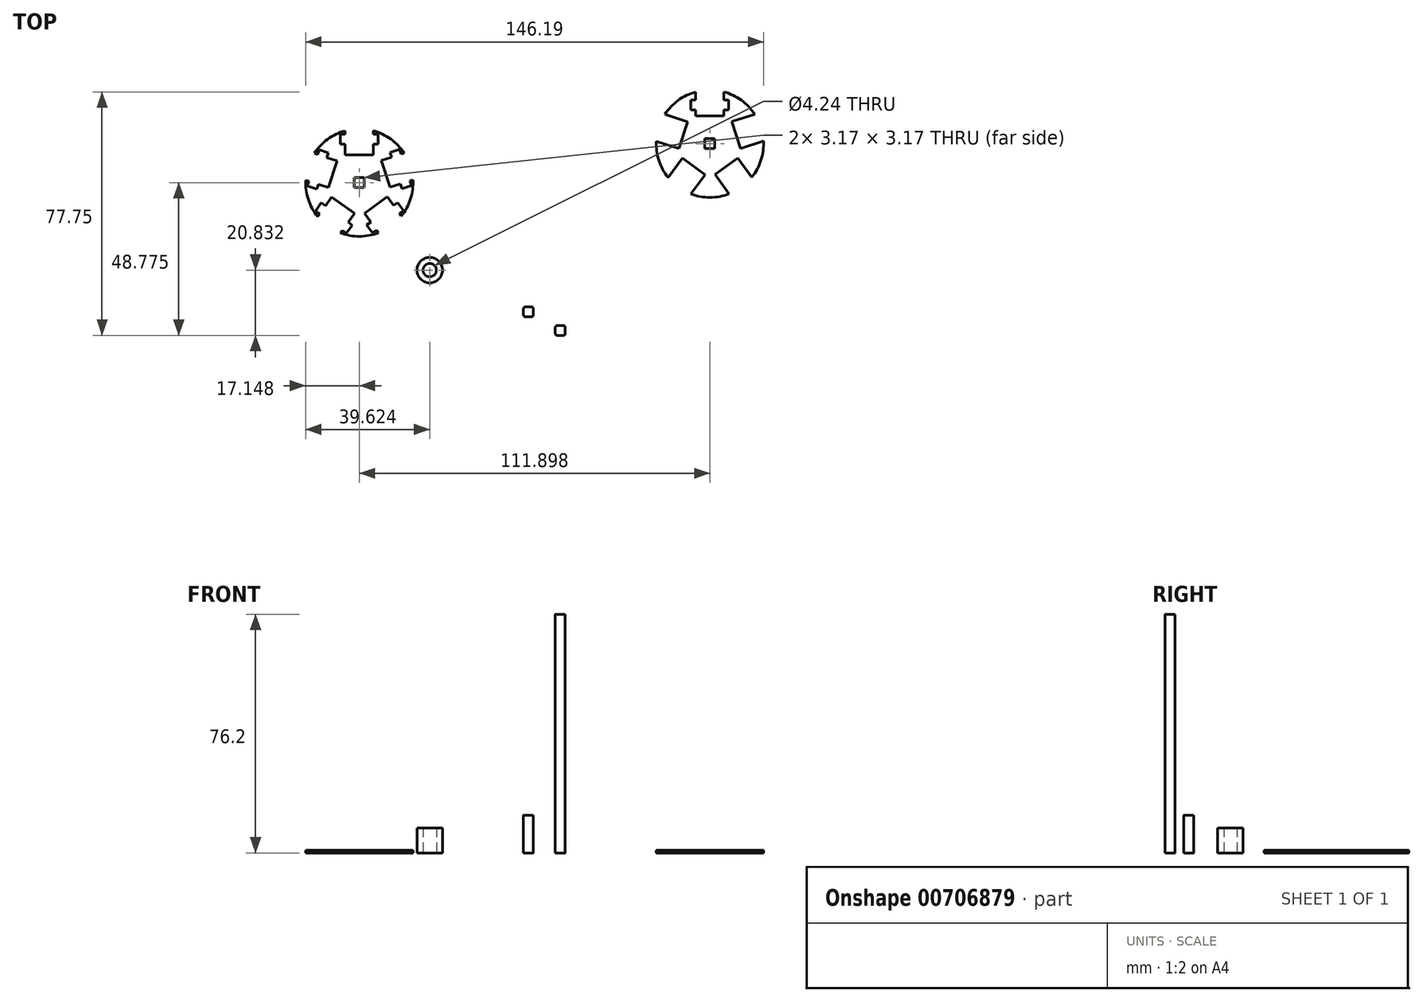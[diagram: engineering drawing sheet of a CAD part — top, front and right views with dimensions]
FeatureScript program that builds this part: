
annotation { "Feature Type Name" : "Feature", "Feature Type Description" : "" }
export const myFeature = defineFeature(function(context is Context, id is Id, definition is map)
    precondition{}
    {
        {
            var Q0;
            Q0=qCreatedBy(makeId("Top.planeOp"),FACE);
            var sketch = newSketch(context, id + "F0", { "sketchPlane" : qUnion([Q0])});
            skCircle(sketch, "E0", {"center": v(-23.39, -16.05) * mm, "radius": 4.06 * mm});
            skCircle(sketch, "E1", {"center": v(-23.39, -16.05) * mm, "radius": 2.12 * mm});
            skLineSegment(sketch, "E2.bottom", {"start": v(-44.27, 10.3) * mm, "end": v(-47.45, 10.3) * mm});
            skLineSegment(sketch, "E2.top", {"start": v(-44.27, 13.48) * mm, "end": v(-47.45, 13.48) * mm});
            skLineSegment(sketch, "E2.left", {"start": v(-44.27, 10.3) * mm, "end": v(-44.27, 13.48) * mm});
            skLineSegment(sketch, "E2.right", {"start": v(-47.45, 10.3) * mm, "end": v(-47.45, 13.48) * mm});
            skPoint(sketch, "E2.middle", {"position": v(-45.86, 11.9) * mm});
            skCircle(sketch, "E3", {"center": v(-45.86, 11.9) * mm, "radius": 17.15 * mm});
            skLineSegment(sketch, "E4.bottom", {"start": v(-41.42, 20.79) * mm, "end": v(-50.42, 20.79) * mm});
            skLineSegment(sketch, "E4.top", {"start": v(-41.42, 37.3) * mm, "end": v(-50.42, 37.3) * mm});
            skLineSegment(sketch, "E4.left", {"start": v(-41.42, 20.79) * mm, "end": v(-41.42, 37.3) * mm});
            skLineSegment(sketch, "E4.right", {"start": v(-50.42, 20.79) * mm, "end": v(-50.42, 37.3) * mm});
            skPoint(sketch, "E4.middle", {"position": v(-45.92, 29.04) * mm});
            skPoint(sketch, "E5.center", {"position": v(-54.13, 17) * mm});
            skLineSegment(sketch, "E6.bottom", {"start": v(-50.42, 27.39) * mm, "end": v(-52, 27.39) * mm});
            skLineSegment(sketch, "E6.top", {"start": v(-50.42, 24.21) * mm, "end": v(-52, 24.21) * mm});
            skLineSegment(sketch, "E6.left", {"start": v(-50.42, 27.39) * mm, "end": v(-50.42, 24.21) * mm});
            skLineSegment(sketch, "E6.right", {"start": v(-52, 27.39) * mm, "end": v(-52, 24.21) * mm});
            skLineSegment(sketch, "E7.bottom", {"start": v(-41.42, 27.39) * mm, "end": v(-39.83, 27.39) * mm});
            skLineSegment(sketch, "E7.top", {"start": v(-41.42, 24.21) * mm, "end": v(-39.83, 24.21) * mm});
            skLineSegment(sketch, "E7.left", {"start": v(-41.42, 27.39) * mm, "end": v(-41.42, 24.21) * mm});
            skLineSegment(sketch, "E7.right", {"start": v(-39.83, 27.39) * mm, "end": v(-39.83, 24.21) * mm});
            skLineSegment(sketch, "E8.1.0", {"start": v(-38.81, 18.97) * mm, "end": v(-23.11, 24.08) * mm});
            skLineSegment(sketch, "E8.1.1", {"start": v(-36.03, 10.41) * mm, "end": v(-20.33, 15.52) * mm});
            skLineSegment(sketch, "E8.1.2", {"start": v(-36.03, 10.41) * mm, "end": v(-38.81, 18.97) * mm});
            skLineSegment(sketch, "E8.1.3", {"start": v(-32.77, 11.47) * mm, "end": v(-32.28, 9.96) * mm});
            skLineSegment(sketch, "E8.1.4", {"start": v(-29.75, 12.46) * mm, "end": v(-29.26, 10.95) * mm});
            skLineSegment(sketch, "E8.1.5", {"start": v(-29.26, 10.95) * mm, "end": v(-32.28, 9.96) * mm});
            skLineSegment(sketch, "E8.1.6", {"start": v(-35.55, 20.03) * mm, "end": v(-36.04, 21.54) * mm});
            skLineSegment(sketch, "E8.1.7", {"start": v(-33.02, 22.52) * mm, "end": v(-36.04, 21.54) * mm});
            skLineSegment(sketch, "E8.1.8", {"start": v(-32.53, 21.01) * mm, "end": v(-33.02, 22.52) * mm});
            skLineSegment(sketch, "E8.2.0", {"start": v(-36.95, 7.38) * mm, "end": v(-27.25, -5.98) * mm});
            skLineSegment(sketch, "E8.2.1", {"start": v(-44.23, 2.1) * mm, "end": v(-34.53, -11.27) * mm});
            skLineSegment(sketch, "E8.2.2", {"start": v(-44.23, 2.1) * mm, "end": v(-36.95, 7.38) * mm});
            skLineSegment(sketch, "E8.2.3", {"start": v(-42.22, -0.68) * mm, "end": v(-43.5, -1.62) * mm});
            skLineSegment(sketch, "E8.2.4", {"start": v(-40.35, -3.25) * mm, "end": v(-41.64, -4.19) * mm});
            skLineSegment(sketch, "E8.2.5", {"start": v(-41.64, -4.19) * mm, "end": v(-43.5, -1.62) * mm});
            skLineSegment(sketch, "E8.2.6", {"start": v(-34.94, 4.6) * mm, "end": v(-33.65, 5.54) * mm});
            skLineSegment(sketch, "E8.2.7", {"start": v(-31.79, 2.97) * mm, "end": v(-33.65, 5.54) * mm});
            skLineSegment(sketch, "E8.2.8", {"start": v(-33.07, 2.04) * mm, "end": v(-31.79, 2.97) * mm});
            skLineSegment(sketch, "E8.3.0", {"start": v(-47.4, 2.03) * mm, "end": v(-57.1, -11.33) * mm});
            skLineSegment(sketch, "E8.3.1", {"start": v(-54.68, 7.32) * mm, "end": v(-64.39, -6.04) * mm});
            skLineSegment(sketch, "E8.3.2", {"start": v(-54.68, 7.32) * mm, "end": v(-47.4, 2.03) * mm});
            skLineSegment(sketch, "E8.3.3", {"start": v(-56.7, 4.54) * mm, "end": v(-57.98, 5.48) * mm});
            skLineSegment(sketch, "E8.3.4", {"start": v(-58.57, 1.97) * mm, "end": v(-59.85, 2.9) * mm});
            skLineSegment(sketch, "E8.3.5", {"start": v(-59.85, 2.9) * mm, "end": v(-57.98, 5.48) * mm});
            skLineSegment(sketch, "E8.3.6", {"start": v(-49.42, -0.75) * mm, "end": v(-48.13, -1.68) * mm});
            skLineSegment(sketch, "E8.3.7", {"start": v(-50, -4.25) * mm, "end": v(-48.13, -1.68) * mm});
            skLineSegment(sketch, "E8.3.8", {"start": v(-51.28, -3.32) * mm, "end": v(-50, -4.25) * mm});
            skLineSegment(sketch, "E8.4.0", {"start": v(-55.72, 10.31) * mm, "end": v(-71.43, 15.41) * mm});
            skLineSegment(sketch, "E8.4.1", {"start": v(-52.94, 18.87) * mm, "end": v(-68.65, 23.97) * mm});
            skLineSegment(sketch, "E8.4.2", {"start": v(-52.94, 18.87) * mm, "end": v(-55.72, 10.31) * mm});
            skLineSegment(sketch, "E8.4.3", {"start": v(-56.2, 19.93) * mm, "end": v(-55.71, 21.44) * mm});
            skLineSegment(sketch, "E8.4.4", {"start": v(-59.22, 20.91) * mm, "end": v(-58.73, 22.42) * mm});
            skLineSegment(sketch, "E8.4.5", {"start": v(-58.73, 22.42) * mm, "end": v(-55.71, 21.44) * mm});
            skLineSegment(sketch, "E8.4.6", {"start": v(-58.99, 11.37) * mm, "end": v(-59.48, 9.86) * mm});
            skLineSegment(sketch, "E8.4.7", {"start": v(-62.5, 10.84) * mm, "end": v(-59.48, 9.86) * mm});
            skLineSegment(sketch, "E8.4.8", {"start": v(-62, 12.35) * mm, "end": v(-62.5, 10.84) * mm});
            skLineSegment(sketch, "E8.anchor1", {"start": v(-45.86, 11.9) * mm, "end": v(-50.42, 20.79) * mm, "construction": true});
            skLineSegment(sketch, "E8.anchor2", {"start": v(-45.86, 11.9) * mm, "end": v(-50.42, 20.79) * mm, "construction": true});
            skLineSegment(sketch, "E9.bottom", {"start": v(67.62, 22.73) * mm, "end": v(64.45, 22.73) * mm});
            skLineSegment(sketch, "E9.top", {"start": v(67.62, 25.9) * mm, "end": v(64.45, 25.9) * mm});
            skLineSegment(sketch, "E9.left", {"start": v(67.62, 22.73) * mm, "end": v(67.62, 25.9) * mm});
            skLineSegment(sketch, "E9.right", {"start": v(64.45, 22.73) * mm, "end": v(64.45, 25.9) * mm});
            skPoint(sketch, "E9.middle", {"position": v(66.04, 24.32) * mm});
            skCircle(sketch, "E10", {"center": v(66.04, 24.32) * mm, "radius": 17.15 * mm});
            skLineSegment(sketch, "E11.bottom", {"start": v(70.48, 33.2) * mm, "end": v(61.48, 33.2) * mm});
            skLineSegment(sketch, "E11.top", {"start": v(70.48, 49.72) * mm, "end": v(61.48, 49.72) * mm});
            skLineSegment(sketch, "E11.left", {"start": v(70.48, 33.2) * mm, "end": v(70.48, 49.72) * mm});
            skLineSegment(sketch, "E11.right", {"start": v(61.48, 33.2) * mm, "end": v(61.48, 49.72) * mm});
            skPoint(sketch, "E11.middle", {"position": v(65.98, 41.46) * mm});
            skPoint(sketch, "E12.center", {"position": v(66.04, 26.86) * mm});
            skLineSegment(sketch, "E13.bottom", {"start": v(61.48, 38.26) * mm, "end": v(59.9, 38.26) * mm});
            skLineSegment(sketch, "E13.top", {"start": v(61.48, 35.09) * mm, "end": v(59.9, 35.09) * mm});
            skLineSegment(sketch, "E13.left", {"start": v(61.48, 38.26) * mm, "end": v(61.48, 35.09) * mm});
            skLineSegment(sketch, "E13.right", {"start": v(59.9, 38.26) * mm, "end": v(59.9, 35.09) * mm});
            skLineSegment(sketch, "E14.bottom", {"start": v(70.48, 38.29) * mm, "end": v(72.07, 38.29) * mm});
            skLineSegment(sketch, "E14.top", {"start": v(70.48, 35.11) * mm, "end": v(72.07, 35.11) * mm});
            skLineSegment(sketch, "E14.left", {"start": v(70.48, 38.29) * mm, "end": v(70.48, 35.11) * mm});
            skLineSegment(sketch, "E14.right", {"start": v(72.07, 38.29) * mm, "end": v(72.07, 35.11) * mm});
            skLineSegment(sketch, "E15.1.0", {"start": v(73.08, 31.4) * mm, "end": v(88.79, 36.5) * mm});
            skLineSegment(sketch, "E15.1.1", {"start": v(75.86, 22.83) * mm, "end": v(91.57, 27.94) * mm});
            skLineSegment(sketch, "E15.1.2", {"start": v(75.86, 22.83) * mm, "end": v(73.08, 31.4) * mm});
            skLineSegment(sketch, "E15.1.3", {"start": v(77.68, 23.42) * mm, "end": v(78.17, 21.91) * mm});
            skLineSegment(sketch, "E15.1.4", {"start": v(80.7, 24.4) * mm, "end": v(81.19, 22.9) * mm});
            skLineSegment(sketch, "E15.1.5", {"start": v(81.19, 22.9) * mm, "end": v(78.17, 21.91) * mm});
            skLineSegment(sketch, "E15.1.6", {"start": v(74.88, 31.98) * mm, "end": v(74.38, 33.49) * mm});
            skLineSegment(sketch, "E15.1.7", {"start": v(77.4, 34.47) * mm, "end": v(74.38, 33.49) * mm});
            skLineSegment(sketch, "E15.1.8", {"start": v(77.9, 32.96) * mm, "end": v(77.4, 34.47) * mm});
            skLineSegment(sketch, "E15.2.0", {"start": v(74.95, 19.8) * mm, "end": v(84.65, 6.44) * mm});
            skLineSegment(sketch, "E15.2.1", {"start": v(67.66, 14.51) * mm, "end": v(77.37, 1.15) * mm});
            skLineSegment(sketch, "E15.2.2", {"start": v(67.66, 14.51) * mm, "end": v(74.95, 19.8) * mm});
            skLineSegment(sketch, "E15.2.3", {"start": v(68.78, 12.97) * mm, "end": v(67.5, 12.04) * mm});
            skLineSegment(sketch, "E15.2.4", {"start": v(70.65, 10.4) * mm, "end": v(69.37, 9.47) * mm});
            skLineSegment(sketch, "E15.2.5", {"start": v(69.37, 9.47) * mm, "end": v(67.5, 12.04) * mm});
            skLineSegment(sketch, "E15.2.6", {"start": v(76.05, 18.28) * mm, "end": v(77.34, 19.2) * mm});
            skLineSegment(sketch, "E15.2.7", {"start": v(79.2, 16.64) * mm, "end": v(77.34, 19.2) * mm});
            skLineSegment(sketch, "E15.2.8", {"start": v(77.92, 15.7) * mm, "end": v(79.2, 16.64) * mm});
            skLineSegment(sketch, "E15.3.0", {"start": v(64.5, 14.45) * mm, "end": v(54.8, 1.09) * mm});
            skLineSegment(sketch, "E15.3.1", {"start": v(57.21, 19.74) * mm, "end": v(47.5, 6.38) * mm});
            skLineSegment(sketch, "E15.3.2", {"start": v(57.21, 19.74) * mm, "end": v(64.5, 14.45) * mm});
            skLineSegment(sketch, "E15.3.3", {"start": v(56.1, 18.2) * mm, "end": v(54.8, 19.13) * mm});
            skLineSegment(sketch, "E15.3.4", {"start": v(54.23, 15.63) * mm, "end": v(52.94, 16.56) * mm});
            skLineSegment(sketch, "E15.3.5", {"start": v(52.94, 16.56) * mm, "end": v(54.8, 19.13) * mm});
            skLineSegment(sketch, "E15.3.6", {"start": v(63.39, 12.92) * mm, "end": v(64.67, 11.99) * mm});
            skLineSegment(sketch, "E15.3.7", {"start": v(62.8, 9.42) * mm, "end": v(64.67, 11.99) * mm});
            skLineSegment(sketch, "E15.3.8", {"start": v(61.52, 10.35) * mm, "end": v(62.8, 9.42) * mm});
            skLineSegment(sketch, "E15.4.0", {"start": v(56.17, 22.73) * mm, "end": v(40.47, 27.83) * mm});
            skLineSegment(sketch, "E15.4.1", {"start": v(58.95, 31.3) * mm, "end": v(43.25, 36.4) * mm});
            skLineSegment(sketch, "E15.4.2", {"start": v(58.95, 31.3) * mm, "end": v(56.17, 22.73) * mm});
            skLineSegment(sketch, "E15.4.3", {"start": v(57.14, 31.88) * mm, "end": v(57.63, 33.39) * mm});
            skLineSegment(sketch, "E15.4.4", {"start": v(54.12, 32.86) * mm, "end": v(54.61, 34.37) * mm});
            skLineSegment(sketch, "E15.4.5", {"start": v(54.61, 34.37) * mm, "end": v(57.63, 33.39) * mm});
            skLineSegment(sketch, "E15.4.6", {"start": v(54.38, 23.31) * mm, "end": v(53.9, 21.8) * mm});
            skLineSegment(sketch, "E15.4.7", {"start": v(50.87, 22.78) * mm, "end": v(53.9, 21.8) * mm});
            skLineSegment(sketch, "E15.4.8", {"start": v(51.36, 24.3) * mm, "end": v(50.87, 22.78) * mm});
            skLineSegment(sketch, "E15.anchor1", {"start": v(66.04, 24.32) * mm, "end": v(61.48, 33.2) * mm, "construction": true});
            skLineSegment(sketch, "E15.anchor2", {"start": v(66.04, 24.32) * mm, "end": v(61.48, 33.2) * mm, "construction": true});
            skLineSegment(sketch, "E16.bottom", {"start": v(9.7, -30.94) * mm, "end": v(6.52, -30.94) * mm});
            skLineSegment(sketch, "E16.top", {"start": v(9.7, -27.76) * mm, "end": v(6.52, -27.76) * mm});
            skLineSegment(sketch, "E16.left", {"start": v(9.7, -30.94) * mm, "end": v(9.7, -27.76) * mm});
            skLineSegment(sketch, "E16.right", {"start": v(6.52, -30.94) * mm, "end": v(6.52, -27.76) * mm});
            skPoint(sketch, "E16.middle", {"position": v(8.1, -29.35) * mm});
            skLineSegment(sketch, "E17.bottom", {"start": v(19.87, -36.88) * mm, "end": v(16.7, -36.88) * mm});
            skLineSegment(sketch, "E17.top", {"start": v(19.87, -33.7) * mm, "end": v(16.7, -33.7) * mm});
            skLineSegment(sketch, "E17.left", {"start": v(19.87, -36.88) * mm, "end": v(19.87, -33.7) * mm});
            skLineSegment(sketch, "E17.right", {"start": v(16.7, -36.88) * mm, "end": v(16.7, -33.7) * mm});
            skPoint(sketch, "E17.middle", {"position": v(18.28, -35.3) * mm});
            skSolve(sketch);
        }
        {
            var Q0;
            Q0=makeQuery(id+"F0.imprint","IMPRINT",FACE,{"disambiguationData":[TD([[makeQuery(id+"F0.imprint","IMPRINT",EDGE,{"derivedFrom":sQuery(id+"F0.wireOp",EDGE,"E9.bottom")}),1.0]])]});
            var Q1;
            {var subQ0=sQuery(id+"F0.wireOp",EDGE,"E13.top");Q1=makeQuery(id+"F0.imprint","IMPRINT",FACE,{"disambiguationData":[TD([[makeQuery(id+"F0.imprint","IMPRINT",EDGE,{"derivedFrom":subQ0}),-1.0]])]});}
            var Q2;
            {var subQ0=sQuery(id+"F0.wireOp",EDGE,"E14.top");Q2=makeQuery(id+"F0.imprint","IMPRINT",FACE,{"disambiguationData":[TD([[makeQuery(id+"F0.imprint","IMPRINT",EDGE,{"derivedFrom":subQ0}),1.0]])]});}
            var Q3;
            {var subQ0=sQuery(id+"F0.wireOp",EDGE,"E15.1.6");Q3=makeQuery(id+"F0.imprint","IMPRINT",FACE,{"disambiguationData":[TD([[makeQuery(id+"F0.imprint","IMPRINT",EDGE,{"derivedFrom":subQ0}),-1.0]])]});}
            var Q4;
            {var subQ0=sQuery(id+"F0.wireOp",EDGE,"E15.1.3");Q4=makeQuery(id+"F0.imprint","IMPRINT",FACE,{"disambiguationData":[TD([[makeQuery(id+"F0.imprint","IMPRINT",EDGE,{"derivedFrom":subQ0}),1.0]])]});}
            var Q5;
            {var subQ0=sQuery(id+"F0.wireOp",EDGE,"E15.2.6");Q5=makeQuery(id+"F0.imprint","IMPRINT",FACE,{"disambiguationData":[TD([[makeQuery(id+"F0.imprint","IMPRINT",EDGE,{"derivedFrom":subQ0}),-1.0]])]});}
            var Q6;
            {var subQ0=sQuery(id+"F0.wireOp",EDGE,"E15.2.3");Q6=makeQuery(id+"F0.imprint","IMPRINT",FACE,{"disambiguationData":[TD([[makeQuery(id+"F0.imprint","IMPRINT",EDGE,{"derivedFrom":subQ0}),1.0]])]});}
            var Q7;
            {var subQ0=sQuery(id+"F0.wireOp",EDGE,"E15.3.6");Q7=makeQuery(id+"F0.imprint","IMPRINT",FACE,{"disambiguationData":[TD([[makeQuery(id+"F0.imprint","IMPRINT",EDGE,{"derivedFrom":subQ0}),-1.0]])]});}
            var Q8;
            {var subQ0=sQuery(id+"F0.wireOp",EDGE,"E15.3.3");Q8=makeQuery(id+"F0.imprint","IMPRINT",FACE,{"disambiguationData":[TD([[makeQuery(id+"F0.imprint","IMPRINT",EDGE,{"derivedFrom":subQ0}),1.0]])]});}
            var Q9;
            {var subQ0=sQuery(id+"F0.wireOp",EDGE,"E15.4.6");Q9=makeQuery(id+"F0.imprint","IMPRINT",FACE,{"disambiguationData":[TD([[makeQuery(id+"F0.imprint","IMPRINT",EDGE,{"derivedFrom":subQ0}),-1.0]])]});}
            var Q10;
            {var subQ0=sQuery(id+"F0.wireOp",EDGE,"E15.4.3");Q10=makeQuery(id+"F0.imprint","IMPRINT",FACE,{"disambiguationData":[TD([[makeQuery(id+"F0.imprint","IMPRINT",EDGE,{"derivedFrom":subQ0}),1.0]])]});}
            var Q11;
            Q11=makeQuery(id+"F0.imprint","IMPRINT",FACE,{"disambiguationData":[TD([[makeQuery(id+"F0.imprint","IMPRINT",EDGE,{"derivedFrom":sQuery(id+"F0.wireOp",EDGE,"E2.bottom")}),1.0]])]});
            extrude(context, id + "F1", {"entities" : qUnion([Q0, Q1, Q2, Q3, Q4, Q5, Q6, Q7, Q8, Q9, Q10, Q11]), "depth" : 0.8 * mm, "offsetDistance" : 25.4 * mm});
        }
        {
            var Q0;
            Q0=makeQuery(id+"F0.imprint","IMPRINT",FACE,{"disambiguationData":[TD([[makeQuery(id+"F0.imprint","IMPRINT",EDGE,{"derivedFrom":sQuery(id+"F0.wireOp",EDGE,"E0")}),1.0]])]});
            extrude(context, id + "F2", {"entities" : qUnion([Q0]), "depth" : 8 * mm, "offsetDistance" : 25.4 * mm});
        }
        {
            var Q0;
            Q0=makeQuery(id+"F0.imprint","IMPRINT",FACE,{"disambiguationData":[TD([[makeQuery(id+"F0.imprint","IMPRINT",EDGE,{"derivedFrom":sQuery(id+"F0.wireOp",EDGE,"E16.bottom")}),-1.0]])]});
            extrude(context, id + "F3", {"entities" : qUnion([Q0]), "depth" : 12.06 * mm, "offsetDistance" : 25.4 * mm});
        }
        {
            var Q0;
            Q0=makeQuery(id+"F0.imprint","IMPRINT",FACE,{"disambiguationData":[TD([[makeQuery(id+"F0.imprint","IMPRINT",EDGE,{"derivedFrom":sQuery(id+"F0.wireOp",EDGE,"E17.bottom")}),-1.0]])]});
            extrude(context, id + "F4", {"entities" : qUnion([Q0]), "depth" : 76.2 * mm, "offsetDistance" : 25.4 * mm});
        }
        {
            var Q0;
            Q0=makeQuery(id+"F3.opExtrude","SWEPT_EDGE",EDGE,{"disambiguationData":[OSD([sQuery(id+"F0.wireOp",EDGE,"E16.bottom"),sQuery(id+"F0.wireOp",EDGE,"E16.left")])]});
            var Q1;
            Q1=makeQuery(id+"F3.opExtrude","SWEPT_EDGE",EDGE,{"disambiguationData":[OSD([sQuery(id+"F0.wireOp",EDGE,"E16.bottom"),sQuery(id+"F0.wireOp",EDGE,"E16.right")])]});
            var Q2;
            Q2=makeQuery(id+"F3.opExtrude","SWEPT_EDGE",EDGE,{"disambiguationData":[OSD([sQuery(id+"F0.wireOp",EDGE,"E16.top"),sQuery(id+"F0.wireOp",EDGE,"E16.left")])]});
            var Q3;
            Q3=makeQuery(id+"F3.opExtrude","SWEPT_EDGE",EDGE,{"disambiguationData":[OSD([sQuery(id+"F0.wireOp",EDGE,"E16.top"),sQuery(id+"F0.wireOp",EDGE,"E16.right")])]});
            var Q4;
            Q4=makeQuery(id+"F4.opExtrude","SWEPT_EDGE",EDGE,{"disambiguationData":[OSD([sQuery(id+"F0.wireOp",EDGE,"E17.bottom"),sQuery(id+"F0.wireOp",EDGE,"E17.left")])]});
            var Q5;
            Q5=makeQuery(id+"F4.opExtrude","SWEPT_EDGE",EDGE,{"disambiguationData":[OSD([sQuery(id+"F0.wireOp",EDGE,"E17.bottom"),sQuery(id+"F0.wireOp",EDGE,"E17.right")])]});
            var Q6;
            Q6=makeQuery(id+"F4.opExtrude","SWEPT_EDGE",EDGE,{"disambiguationData":[OSD([sQuery(id+"F0.wireOp",EDGE,"E17.top"),sQuery(id+"F0.wireOp",EDGE,"E17.left")])]});
            var Q7;
            Q7=makeQuery(id+"F4.opExtrude","SWEPT_EDGE",EDGE,{"disambiguationData":[OSD([sQuery(id+"F0.wireOp",EDGE,"E17.top"),sQuery(id+"F0.wireOp",EDGE,"E17.right")])]});
            fillet(context, id + "F5", {"entities" : qUnion([Q0, Q1, Q2, Q3, Q4, Q5, Q6, Q7]), "radius" : 0.64 * mm, "tangentPropagation" : true, "allowEdgeOverflow" : false});
        }
    });
